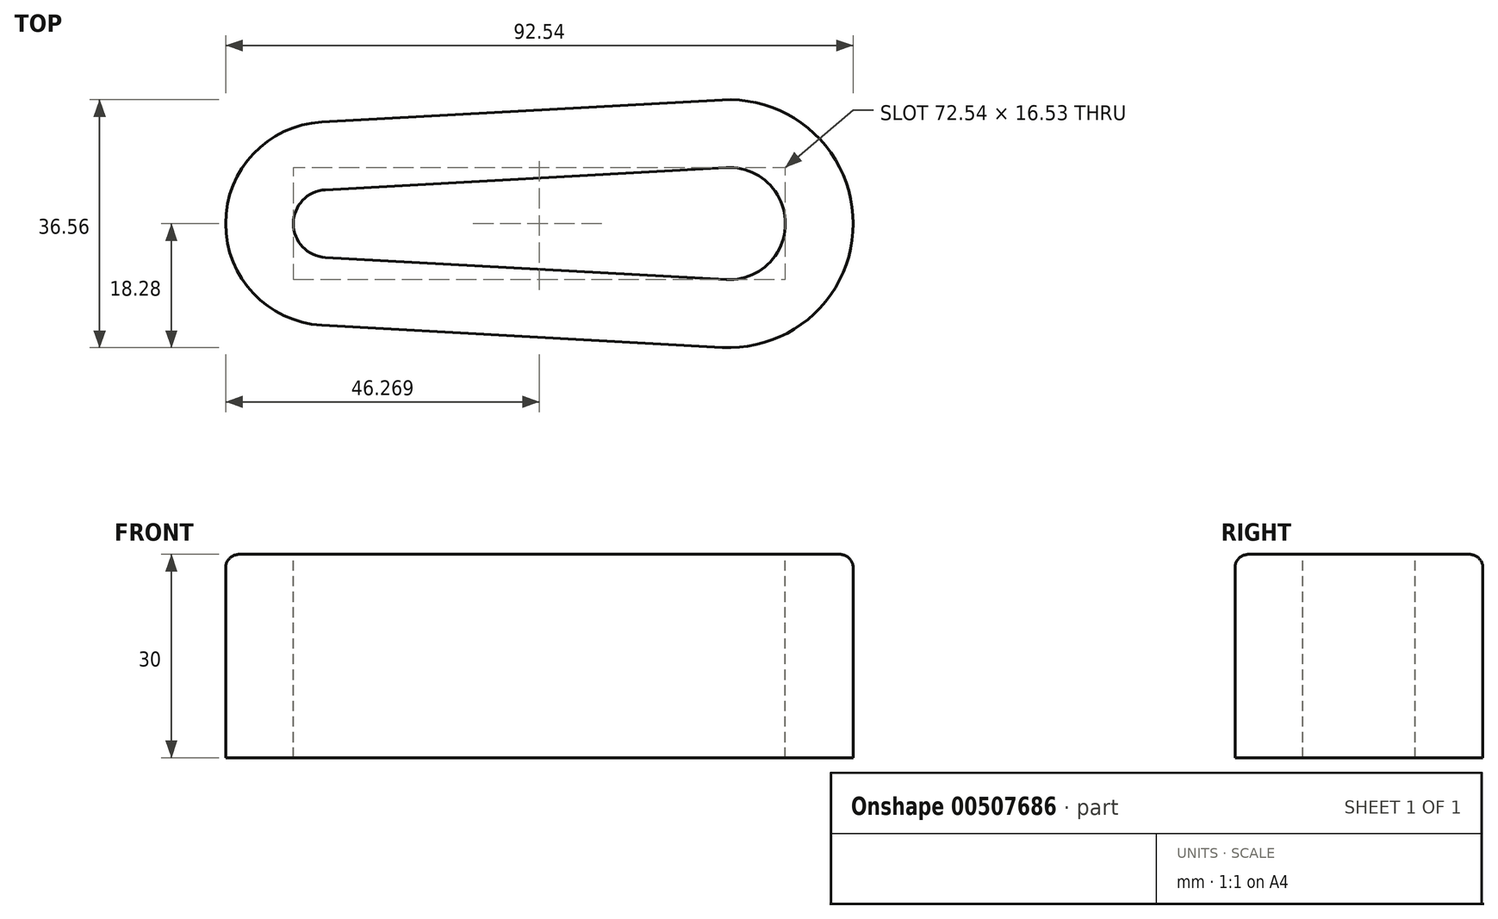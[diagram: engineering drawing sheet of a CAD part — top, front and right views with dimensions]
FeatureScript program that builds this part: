
annotation { "Feature Type Name" : "Feature", "Feature Type Description" : "" }
export const myFeature = defineFeature(function(context is Context, id is Id, definition is map)
    precondition{}
    {
        {
            var Q0;
            Q0=qCreatedBy(makeId("Top.planeOp"),FACE);
            var sketch = newSketch(context, id + "F0", { "sketchPlane" : qUnion([Q0])});
            skArc(sketch, "E0", {"start": v(-44.45, 14.98) * mm, "mid": v(-58.62, 0) * mm, "end": v(-44.45, -14.98) * mm});
            skArc(sketch, "E1", {"start": v(14.63, -18.25) * mm, "mid": v(33.92, 0) * mm, "end": v(14.63, 18.25) * mm});
            skLineSegment(sketch, "E2", {"start": v(-44.45, 14.98) * mm, "end": v(14.63, 18.25) * mm});
            skLineSegment(sketch, "E3", {"start": v(-66.93, 0) * mm, "end": v(53.56, 0) * mm, "construction": true});
            skLineSegment(sketch, "E4.MirrorCS", {"start": v(-44.45, -14.98) * mm, "end": v(14.63, -18.25) * mm});
            skPoint(sketch, "E5.orphan", {"position": v(-58.3, 14.21) * mm});
            skPoint(sketch, "E6.orphan", {"position": v(-58.3, -14.21) * mm});
            skPoint(sketch, "E7.orphan", {"position": v(23.7, 18.75) * mm});
            skPoint(sketch, "E8.orphan", {"position": v(23.7, -18.75) * mm});
            skSolve(sketch);
        }
        {
            var Q0;
            Q0=makeQuery(id+"F0.imprint","IMPRINT",FACE,{"disambiguationData":[TD([[makeQuery(id+"F0.imprint","IMPRINT",EDGE,{"derivedFrom":sQuery(id+"F0.wireOp",EDGE,"E0")}),1.0]])]});
            extrude(context, id + "F1", {"entities" : qUnion([Q0]), "depth" : 30 * mm});
        }
        {
            var Q0;
            Q0=makeQuery(id+"F1.opExtrude","CAP_FACE",FACE,{"disambiguationData":[OSD([sQuery(id+"F0.wireOp",EDGE,"E0"),sQuery(id+"F0.wireOp",EDGE,"E1"),sQuery(id+"F0.wireOp",EDGE,"E2"),sQuery(id+"F0.wireOp",EDGE,"E4.MirrorCS")])],"isStart":false});
            var sketch = newSketch(context, id + "F2", { "sketchPlane" : qUnion([Q0])});
            skLineSegment(sketch, "E9.0", {"start": v(-43.9, -5) * mm, "end": v(15.19, -8.27) * mm});
            skArc(sketch, "E9.1", {"start": v(-43.9, 5) * mm, "mid": v(-48.62, 0) * mm, "end": v(-43.9, -5) * mm});
            skLineSegment(sketch, "E9.2", {"start": v(15.19, 8.27) * mm, "end": v(-43.9, 5) * mm});
            skArc(sketch, "E9.3", {"start": v(15.19, -8.27) * mm, "mid": v(23.92, 0) * mm, "end": v(15.19, 8.27) * mm});
            skSolve(sketch);
        }
        {
            var Q0;
            Q0=makeQuery(id+"F2.imprint","IMPRINT",FACE,{"disambiguationData":[TD([[makeQuery(id+"F2.imprint","IMPRINT",EDGE,{"derivedFrom":sQuery(id+"F2.wireOp",EDGE,"E9.0")}),1.0]])]});
            extrude(context, id + "F3", {"entities" : qUnion([Q0]), "operationType" : NewBodyOperationType.REMOVE, "oppositeDirection" : true, "depth" : 30 * mm});
        }
        {
            var Q0;
            Q0=makeQuery(id+"F3.boolean.opBoolean","COPY",EDGE,{"derivedFrom":makeQuery(id+"F3.opExtrude","CAP_EDGE",EDGE,{"disambiguationData":[OSD([sQuery(id+"F2.wireOp",EDGE,"E9.1")])],"isStart":true})});
            var Q1;
            Q1=makeQuery(id+"F3.boolean.opBoolean","COPY",EDGE,{"derivedFrom":makeQuery(id+"F3.opExtrude","CAP_EDGE",EDGE,{"disambiguationData":[OSD([sQuery(id+"F2.wireOp",EDGE,"E9.3")])],"isStart":true})});
            var Q2;
            Q2=makeQuery(id+"F3.boolean.opBoolean","COPY",EDGE,{"derivedFrom":makeQuery(id+"F3.opExtrude","CAP_EDGE",EDGE,{"disambiguationData":[OSD([sQuery(id+"F2.wireOp",EDGE,"E9.2")])],"isStart":true})});
            var Q3;
            Q3=makeQuery(id+"F1.opExtrude","CAP_EDGE",EDGE,{"disambiguationData":[OSD([sQuery(id+"F0.wireOp",EDGE,"E4.MirrorCS")])],"isStart":false});
            var Q4;
            Q4=makeQuery(id+"F1.opExtrude","CAP_EDGE",EDGE,{"disambiguationData":[OSD([sQuery(id+"F0.wireOp",EDGE,"E1")])],"isStart":false});
            var Q5;
            Q5=makeQuery(id+"F1.opExtrude","CAP_EDGE",EDGE,{"disambiguationData":[OSD([sQuery(id+"F0.wireOp",EDGE,"E2")])],"isStart":false});
            var Q6;
            Q6=makeQuery(id+"F1.opExtrude","CAP_EDGE",EDGE,{"disambiguationData":[OSD([sQuery(id+"F0.wireOp",EDGE,"E0")])],"isStart":false});
            var Q7;
            Q7=makeQuery(id+"F3.boolean.opBoolean","COPY",EDGE,{"derivedFrom":makeQuery(id+"F3.opExtrude","CAP_EDGE",EDGE,{"disambiguationData":[OSD([sQuery(id+"F2.wireOp",EDGE,"E9.0")])],"isStart":true})});
            fillet(context, id + "F4", {"entities" : qUnion([Q0, Q1, Q2, Q3, Q4, Q5, Q6, Q7]), "radius" : 2 * mm, "tangentPropagation" : true, "allowEdgeOverflow" : false});
        }
    });
